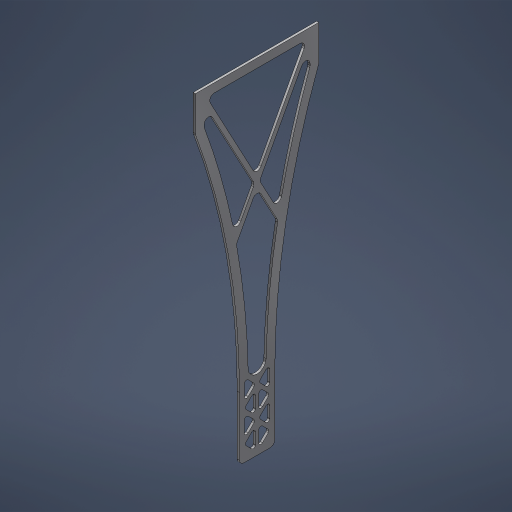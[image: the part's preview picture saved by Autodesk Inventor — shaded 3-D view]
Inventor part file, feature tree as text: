
AUTODESK INVENTOR PART (.ipt)
format: ipt  version: 2024.3 (Build 283343000, 343)  size: 466,432 bytes
history: native  units: mm (DEFAULTED — no unit token found)
features: sheet_metal_op x3, sketch x3, other x3, mirror x2, chamfer x2, projected_geometry x1
ambient origin geometry x8: Origin, YZ Plane, XZ Plane, XY Plane, X Axis, Y Axis, Z Axis, Center Point
bodies: Body1 (feature_tree)
feature tree (14):
  sheet_metal_op  "Face1"
  sheet_metal_op  "Face2"
  mirror  "Mirror2"
  mirror  "Mirror3"
  chamfer  "Corner Round3"
  chamfer  "Corner Round2"
  sketch  "Sketch2"  dims[d6=177.8mm]
  other  "Plate1"
  sketch  "Sketch5"  dims[d7=596.9mm]
  projected_geometry  "Projected Loop2"
  other  "Plate3"
  sheet_metal_op  "Bend2"
  sketch  "Sketch6"  dims[d10=50.8mm d11=25.4mm d12=127.0mm d13=3.175mm d53=1016.0mm d54=12.7mm d59=6.35mm d60=4.7625mm d61=3.175mm d62=1.5875mm d63=6.35mm d64=4.7625mm d65=355.6mm d66=6.35mm d67=15.875mm d68=2.38125mm d69=7.14375mm d70=4.7625mm d71=38.485192mm d72=6.735192mm d73=20.0mm d75=45.220384mm d76=10.0mm d78=25.4mm d80=6.35mm d81=3.175mm d82=0.0mm d83=3.175mm]
  other  "Cut3"
